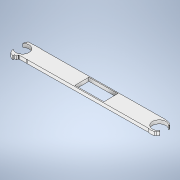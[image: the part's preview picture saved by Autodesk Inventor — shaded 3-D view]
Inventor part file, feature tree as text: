
AUTODESK INVENTOR PART (.ipt)
format: ipt  version: 2022 (Build 260153000, 153)  size: 333,312 bytes
history: native  units: mm
features: extrude x1, sketch x1
ambient origin geometry x8: Origin, YZ Plane, XZ Plane, XY Plane, X Axis, Y Axis, Z Axis, Center Point
bodies: Body1 (feature_tree)
feature tree (2):
  extrude  "Extrusion6"  Depth=20.0mm
  sketch  "Sketch1"  dims[d31=34.456mm d50=368.759386mm d57=16.0mm d69=8.0mm d70=23.0mm d71=8.0mm d73=16.0mm d80=19.0mm d81=16.0mm d82=1.0mm d83=1.0mm d84=1.0mm d85=1.0mm d86=1.0mm d87=0.8mm d88=1.0mm d90=19.0mm d94=5.0mm d95=5.0mm d105=5.0mm d106=5.0mm d108=2.0mm d109=19.0mm d114=5.0mm d115=5.0mm d116=24.0mm d117=2.5mm d118=2.5mm d123=2.5mm d124=2.5mm d125=10.0mm d126=24.0mm d127=24.0mm d128=27.0mm d135=0.5mm d136=45.0deg d139=7.0mm d165=45.0deg d169=27.0mm d175=90.0deg d181=45.0deg d185=7.0mm d186=45.0deg d190=7.0mm d191=45.0deg d197=90.0deg d203=90.0deg d206=7.0mm d209=40.0mm d210=5.0mm d211=0.0mm d212=41.0mm d213=20.0mm d214=23.0mm]
